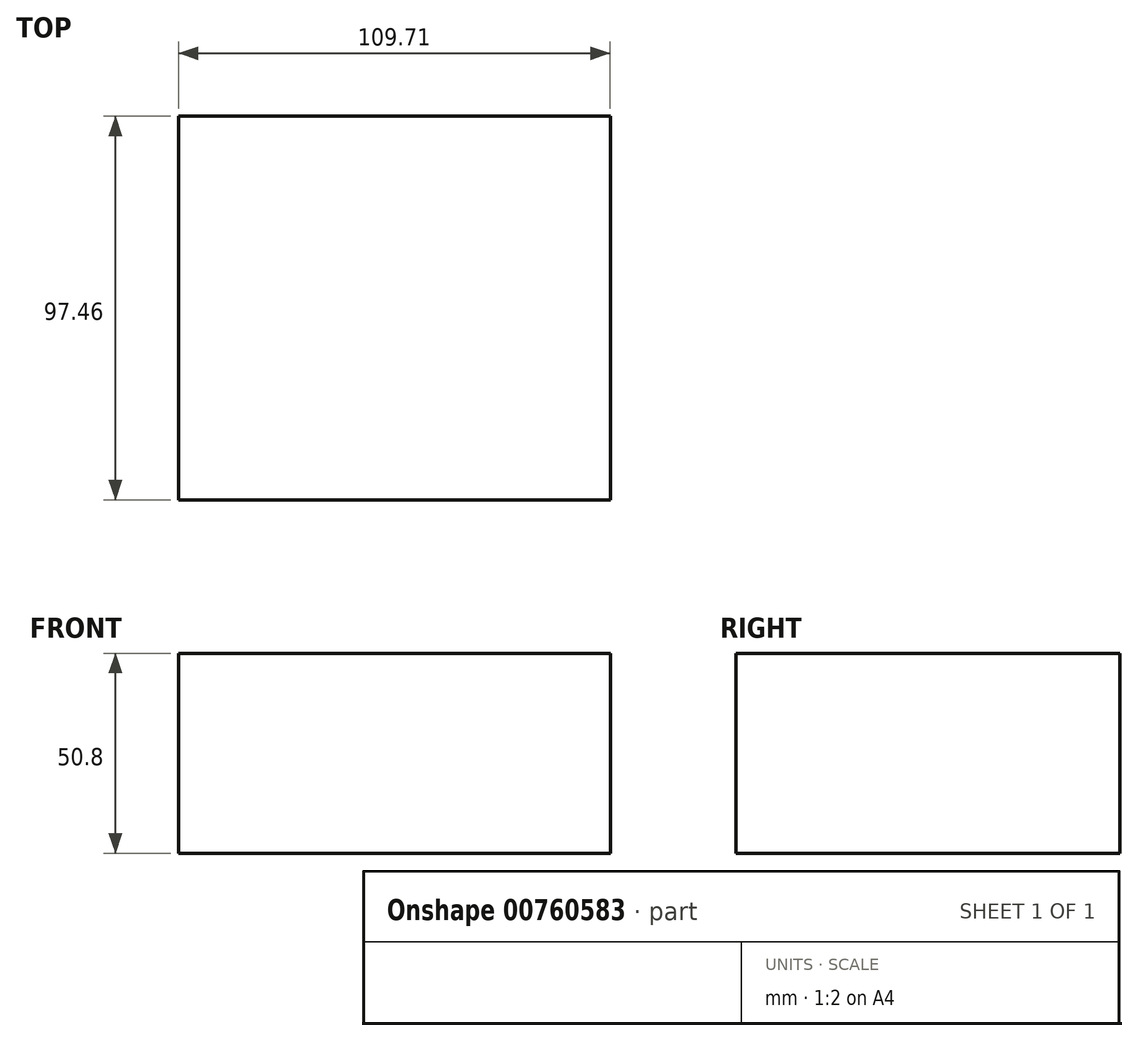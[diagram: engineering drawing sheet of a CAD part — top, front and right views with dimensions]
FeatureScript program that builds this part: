
annotation { "Feature Type Name" : "Feature", "Feature Type Description" : "" }
export const myFeature = defineFeature(function(context is Context, id is Id, definition is map)
    precondition{}
    {
        {
            var Q0;
            Q0=qCreatedBy(makeId("Top.planeOp"),FACE);
            var sketch = newSketch(context, id + "F0", { "sketchPlane" : qUnion([Q0])});
            skLineSegment(sketch, "E0.bottom", {"start": v(-57.36, 43.08) * mm, "end": v(52.35, 43.08) * mm});
            skLineSegment(sketch, "E0.top", {"start": v(-57.36, -54.38) * mm, "end": v(52.35, -54.38) * mm});
            skLineSegment(sketch, "E0.left", {"start": v(-57.36, 43.08) * mm, "end": v(-57.36, -54.38) * mm});
            skLineSegment(sketch, "E0.right", {"start": v(52.35, 43.08) * mm, "end": v(52.35, -54.38) * mm});
            skSolve(sketch);
        }
        {
            var Q0;
            Q0=makeQuery(id+"F0.imprint","IMPRINT",FACE,{"disambiguationData":[TD([[makeQuery(id+"F0.imprint","IMPRINT",EDGE,{"derivedFrom":sQuery(id+"F0.wireOp",EDGE,"E0.bottom")}),-1.0]])]});
            extrude(context, id + "F1", {"entities" : qUnion([Q0]), "depth" : 50.8 * mm, "offsetDistance" : 25.4 * mm});
        }
    });
